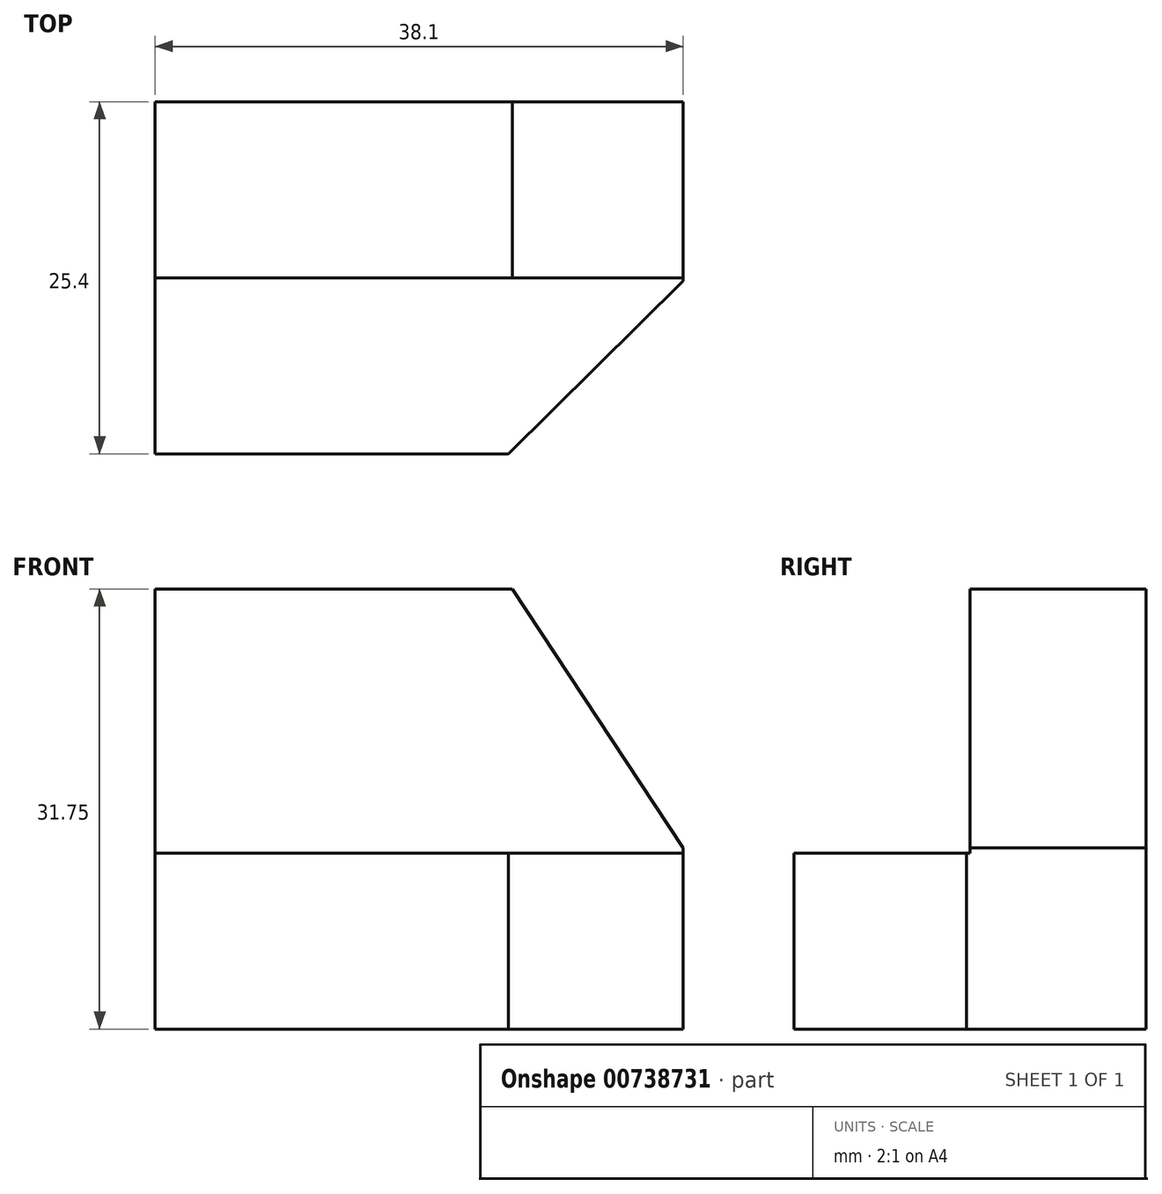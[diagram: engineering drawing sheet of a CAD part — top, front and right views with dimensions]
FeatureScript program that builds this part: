
annotation { "Feature Type Name" : "Feature", "Feature Type Description" : "" }
export const myFeature = defineFeature(function(context is Context, id is Id, definition is map)
    precondition{}
    {
        {
            var Q0;
            Q0=qCreatedBy(makeId("Right.planeOp"),FACE);
            var sketch = newSketch(context, id + "F0", { "sketchPlane" : qUnion([Q0])});
            skLineSegment(sketch, "E0", {"start": v(0, 0) * mm, "end": v(25.4, 0) * mm});
            skLineSegment(sketch, "E1", {"start": v(25.4, 0) * mm, "end": v(25.4, 31.75) * mm});
            skLineSegment(sketch, "E2", {"start": v(25.4, 31.75) * mm, "end": v(12.7, 31.75) * mm});
            skLineSegment(sketch, "E3", {"start": v(12.7, 31.75) * mm, "end": v(12.7, 12.7) * mm});
            skLineSegment(sketch, "E4", {"start": v(12.7, 12.7) * mm, "end": v(0, 12.7) * mm});
            skLineSegment(sketch, "E5", {"start": v(0, 12.7) * mm, "end": v(0, 0) * mm});
            skSolve(sketch);
        }
        {
            var Q0;
            Q0 = qSketchRegion(id + "F0", true);
            extrude(context, id + "F1", {"entities" : qUnion([Q0]), "depth" : 38.1 * mm, "offsetDistance" : 25.4 * mm});
        }
        {
            var Q0;
            Q0=qCreatedBy(makeId("Front.planeOp"),FACE);
            var sketch = newSketch(context, id + "F2", { "sketchPlane" : qUnion([Q0])});
            skLineSegment(sketch, "E6", {"start": v(38.23, 31.92) * mm, "end": v(38.23, 12.87) * mm});
            skLineSegment(sketch, "E7", {"start": v(38.23, 12.87) * mm, "end": v(25.53, 32.1) * mm});
            skLineSegment(sketch, "E8", {"start": v(25.53, 32.1) * mm, "end": v(38.23, 31.92) * mm});
            skSolve(sketch);
        }
        {
            var Q0;
            Q0 = qSketchRegion(id + "F2", true);
            extrude(context, id + "F3", {"entities" : qUnion([Q0]), "operationType" : NewBodyOperationType.REMOVE, "oppositeDirection" : true, "depth" : 25.4 * mm, "offsetDistance" : 25.4 * mm});
        }
        {
            var Q0;
            Q0=qCreatedBy(makeId("Top.planeOp"),FACE);
            var sketch = newSketch(context, id + "F4", { "sketchPlane" : qUnion([Q0])});
            skLineSegment(sketch, "E9", {"start": v(38.35, 12.7) * mm, "end": v(25.49, 0) * mm});
            skLineSegment(sketch, "E10", {"start": v(25.49, 0) * mm, "end": v(38.19, 0) * mm});
            skLineSegment(sketch, "E11", {"start": v(38.19, 0) * mm, "end": v(38.35, 12.7) * mm});
            skSolve(sketch);
        }
        {
            var Q0;
            Q0 = qSketchRegion(id + "F4", true);
            extrude(context, id + "F5", {"entities" : qUnion([Q0]), "operationType" : NewBodyOperationType.REMOVE, "depth" : 25.4 * mm, "offsetDistance" : 25.4 * mm});
        }
    });
